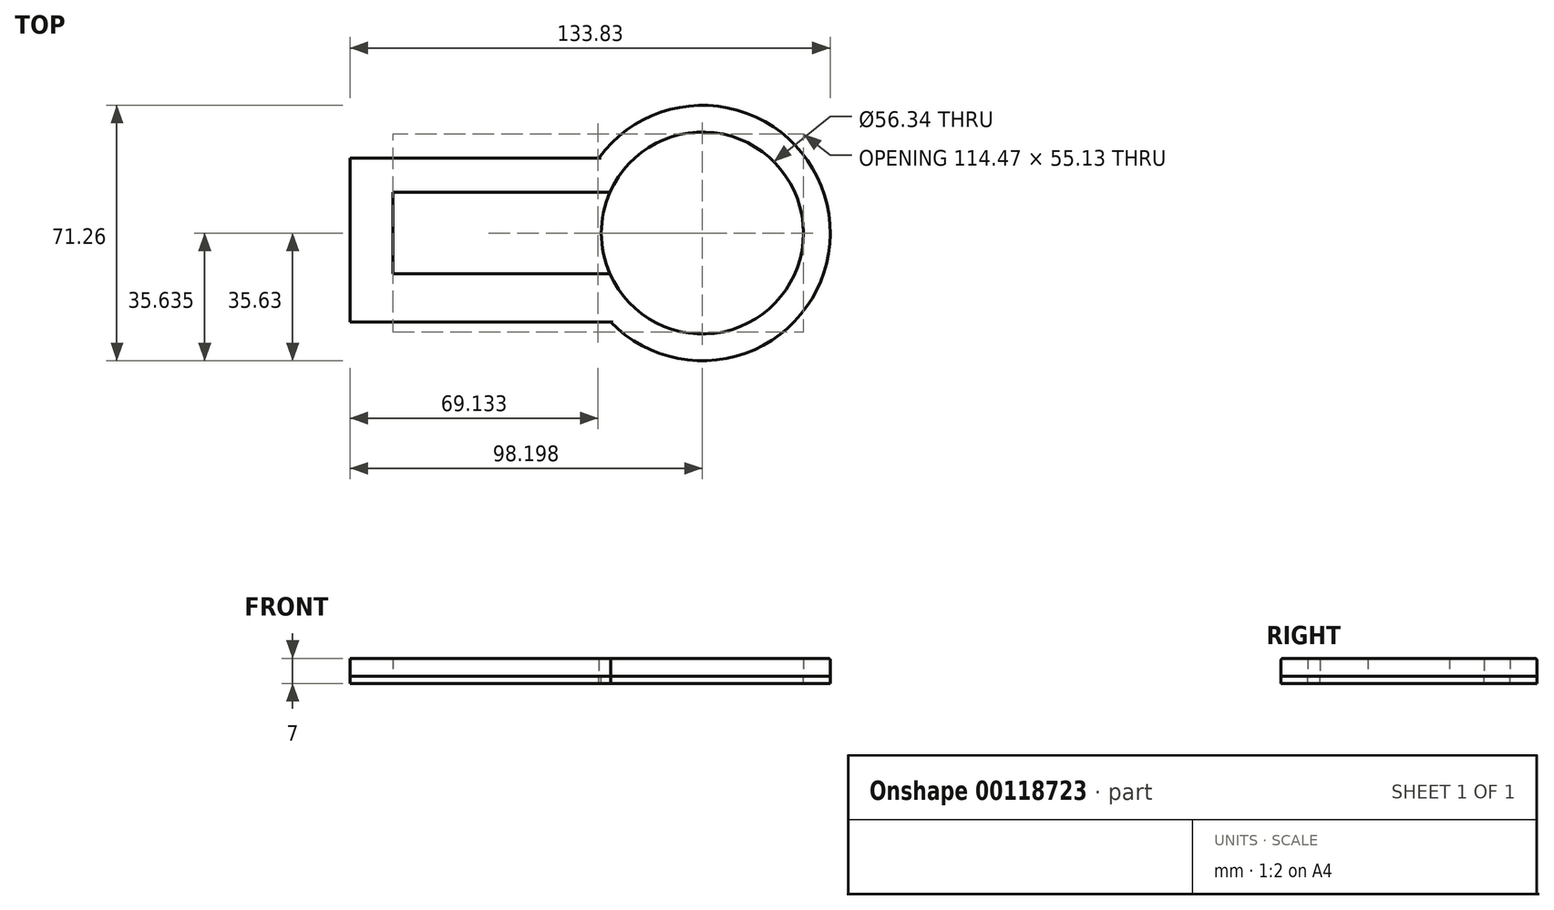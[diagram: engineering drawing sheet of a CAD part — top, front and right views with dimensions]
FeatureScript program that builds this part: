
annotation { "Feature Type Name" : "Feature", "Feature Type Description" : "" }
export const myFeature = defineFeature(function(context is Context, id is Id, definition is map)
    precondition{}
    {
        {
            var Q0;
            Q0=qCreatedBy(makeId("Top.planeOp"),FACE);
            var sketch = newSketch(context, id + "F0", { "sketchPlane" : qUnion([Q0])});
            skLineSegment(sketch, "E0.bottom", {"start": v(40.97, -24.8) * mm, "end": v(-31.65, -24.8) * mm});
            skLineSegment(sketch, "E0.top", {"start": v(40.97, 20.96) * mm, "end": v(-31.65, 20.96) * mm});
            skLineSegment(sketch, "E0.left", {"start": v(40.97, -24.8) * mm, "end": v(40.97, 20.96) * mm});
            skLineSegment(sketch, "E0.right", {"start": v(-31.65, -24.8) * mm, "end": v(-31.65, 20.96) * mm});
            skLineSegment(sketch, "E1.bottom", {"start": v(40.97, -11.36) * mm, "end": v(-19.75, -11.36) * mm});
            skLineSegment(sketch, "E1.top", {"start": v(40.97, 11.32) * mm, "end": v(-19.75, 11.32) * mm});
            skLineSegment(sketch, "E1.left", {"start": v(40.97, -11.36) * mm, "end": v(40.97, 11.32) * mm});
            skLineSegment(sketch, "E1.right", {"start": v(-19.75, -11.36) * mm, "end": v(-19.75, 11.32) * mm});
            skCircle(sketch, "E2", {"center": v(66.55, 0) * mm, "radius": 35.63 * mm});
            skCircle(sketch, "E3", {"center": v(66.55, 0) * mm, "radius": 28.17 * mm});
            skSolve(sketch);
        }
        {
            var Q0;
            {var subQ1=sQuery(id+"F0.wireOp",EDGE,"E0.left");var subQ3=sQuery(id+"F0.wireOp",EDGE,"E0.top");var subQ5=makeQuery(id+"F0.imprint","INTERSECT",VERTEX,{"derivedFrom":[subQ3,subQ1]});Q0=makeQuery(id+"F0.imprint","IMPRINT",FACE,{"disambiguationData":[TD([[makeQuery(id+"F0.imprint","IMPRINT",EDGE,{"disambiguationData":[TD([[subQ5,-1.0]])],"derivedFrom":subQ3}),-1.0]])]});}
            var Q1;
            {var subQ3=sQuery(id+"F0.wireOp",EDGE,"E3");var subQ5=sQuery(id+"F0.wireOp",EDGE,"E1.bottom");var subQ7=makeQuery(id+"F0.imprint","INTERSECT",VERTEX,{"derivedFrom":[subQ5,subQ3]});Q1=makeQuery(id+"F0.imprint","IMPRINT",FACE,{"disambiguationData":[TD([[makeQuery(id+"F0.imprint","IMPRINT",EDGE,{"disambiguationData":[TD([[subQ7,-1.0]])],"derivedFrom":subQ5}),1.0]])]});}
            var Q2;
            {var subQ5=sQuery(id+"F0.wireOp",EDGE,"E0.bottom");Q2=makeQuery(id+"F0.imprint","IMPRINT",FACE,{"disambiguationData":[TD([[makeQuery(id+"F0.imprint","IMPRINT",EDGE,{"derivedFrom":subQ5}),-1.0]])]});}
            var Q3;
            {var subQ5=sQuery(id+"F0.wireOp",EDGE,"E0.top");var subQ7=sQuery(id+"F0.wireOp",EDGE,"E0.left");var subQ8=makeQuery(id+"F0.imprint","INTERSECT",VERTEX,{"derivedFrom":[subQ5,subQ7]});Q3=makeQuery(id+"F0.imprint","IMPRINT",FACE,{"disambiguationData":[TD([[makeQuery(id+"F0.imprint","IMPRINT",EDGE,{"disambiguationData":[TD([[subQ8,-1.0]])],"derivedFrom":subQ5}),1.0]])]});}
            extrude(context, id + "F1", {"entities" : qUnion([Q0, Q1, Q2, Q3]), "depth" : 5 * mm});
        }
        {
            var Q0;
            {var subQ0=sQuery(id+"F0.wireOp",EDGE,"E1.left");Q0=makeQuery(id+"F0.imprint","IMPRINT",FACE,{"disambiguationData":[TD([[makeQuery(id+"F0.imprint","IMPRINT",EDGE,{"derivedFrom":subQ0}),-1.0]])]});}
            var Q1;
            {var subQ0=sQuery(id+"F0.wireOp",EDGE,"E1.right");Q1=makeQuery(id+"F0.imprint","IMPRINT",FACE,{"disambiguationData":[TD([[makeQuery(id+"F0.imprint","IMPRINT",EDGE,{"derivedFrom":subQ0}),-1.0]])]});}
            var Q2;
            {var subQ0=sQuery(id+"F0.wireOp",EDGE,"E1.left");Q2=makeQuery(id+"F0.imprint","IMPRINT",FACE,{"disambiguationData":[TD([[makeQuery(id+"F0.imprint","IMPRINT",EDGE,{"derivedFrom":subQ0}),1.0]])]});}
            var Q3;
            {var subQ3=sQuery(id+"F0.wireOp",EDGE,"E3");var subQ5=sQuery(id+"F0.wireOp",EDGE,"E1.bottom");var subQ7=makeQuery(id+"F0.imprint","INTERSECT",VERTEX,{"derivedFrom":[subQ5,subQ3]});Q3=makeQuery(id+"F0.imprint","IMPRINT",FACE,{"disambiguationData":[TD([[makeQuery(id+"F0.imprint","IMPRINT",EDGE,{"disambiguationData":[TD([[subQ7,-1.0]])],"derivedFrom":subQ5}),1.0]])]});}
            var Q4;
            {var subQ5=sQuery(id+"F0.wireOp",EDGE,"E0.bottom");Q4=makeQuery(id+"F0.imprint","IMPRINT",FACE,{"disambiguationData":[TD([[makeQuery(id+"F0.imprint","IMPRINT",EDGE,{"derivedFrom":subQ5}),-1.0]])]});}
            var Q5;
            {var subQ5=sQuery(id+"F0.wireOp",EDGE,"E0.top");var subQ7=sQuery(id+"F0.wireOp",EDGE,"E0.left");var subQ8=makeQuery(id+"F0.imprint","INTERSECT",VERTEX,{"derivedFrom":[subQ5,subQ7]});Q5=makeQuery(id+"F0.imprint","IMPRINT",FACE,{"disambiguationData":[TD([[makeQuery(id+"F0.imprint","IMPRINT",EDGE,{"disambiguationData":[TD([[subQ8,-1.0]])],"derivedFrom":subQ5}),1.0]])]});}
            var Q6;
            {var subQ1=sQuery(id+"F0.wireOp",EDGE,"E0.left");var subQ3=sQuery(id+"F0.wireOp",EDGE,"E0.top");var subQ5=makeQuery(id+"F0.imprint","INTERSECT",VERTEX,{"derivedFrom":[subQ3,subQ1]});Q6=makeQuery(id+"F0.imprint","IMPRINT",FACE,{"disambiguationData":[TD([[makeQuery(id+"F0.imprint","IMPRINT",EDGE,{"disambiguationData":[TD([[subQ5,-1.0]])],"derivedFrom":subQ3}),-1.0]])]});}
            var Q7;
            {var subQ0=sQuery(id+"F0.wireOp",EDGE,"E3");var subQ1=sQuery(id+"F0.wireOp",EDGE,"E1.bottom");var subQ2=makeQuery(id+"F0.imprint","INTERSECT",VERTEX,{"derivedFrom":[subQ1,subQ0]});Q7=makeQuery(id+"F0.imprint","IMPRINT",FACE,{"disambiguationData":[TD([[makeQuery(id+"F0.imprint","IMPRINT",EDGE,{"disambiguationData":[TD([[subQ2,-1.0]])],"derivedFrom":subQ1}),-1.0]])]});}
            extrude(context, id + "F2", {"entities" : qUnion([Q0, Q1, Q2, Q3, Q4, Q5, Q6, Q7]), "oppositeDirection" : true, "depth" : 2 * mm});
        }
        {
            var Q0;
            Q0=makeQuery(id+"F1.opExtrude","CAP_EDGE",EDGE,{"disambiguationData":[OSD([sQuery(id+"F0.wireOp",EDGE,"E2")])],"isStart":false});
            fillet(context, id + "F3", {"entities" : qUnion([Q0]), "radius" : .5 * mm, "tangentPropagation" : true, "allowEdgeOverflow" : false});
        }
    });
